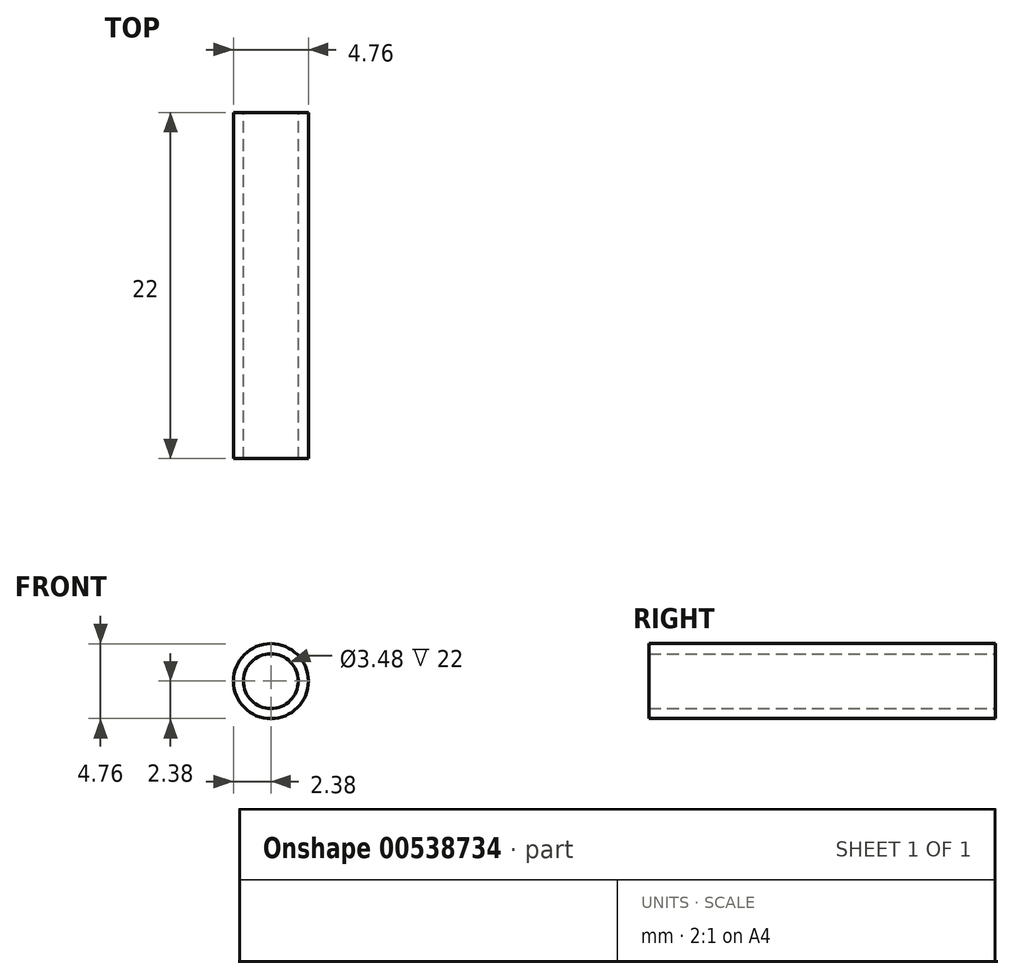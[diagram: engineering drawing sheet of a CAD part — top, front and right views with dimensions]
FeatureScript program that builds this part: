
annotation { "Feature Type Name" : "Feature", "Feature Type Description" : "" }
export const myFeature = defineFeature(function(context is Context, id is Id, definition is map)
    precondition{}
    {
        {
            var Q0;
            Q0=qCreatedBy(makeId("Front.planeOp"),FACE);
            var sketch = newSketch(context, id + "F0", { "sketchPlane" : qUnion([Q0])});
            skCircle(sketch, "E0", {"center": v(0, 0) * mm, "radius": 1.74 * mm});
            skCircle(sketch, "E1", {"center": v(0, 0) * mm, "radius": 2.38 * mm});
            skSolve(sketch);
        }
        {
            var Q0;
            Q0=makeQuery(id+"F0.imprint","IMPRINT",FACE,{"disambiguationData":[TD([[makeQuery(id+"F0.imprint","IMPRINT",EDGE,{"derivedFrom":sQuery(id+"F0.wireOp",EDGE,"E0")}),-1.0]])]});
            extrude(context, id + "F1", {"entities" : qUnion([Q0]), "depth" : 22 * mm, "offsetDistance" : 25 * mm});
        }
    });
